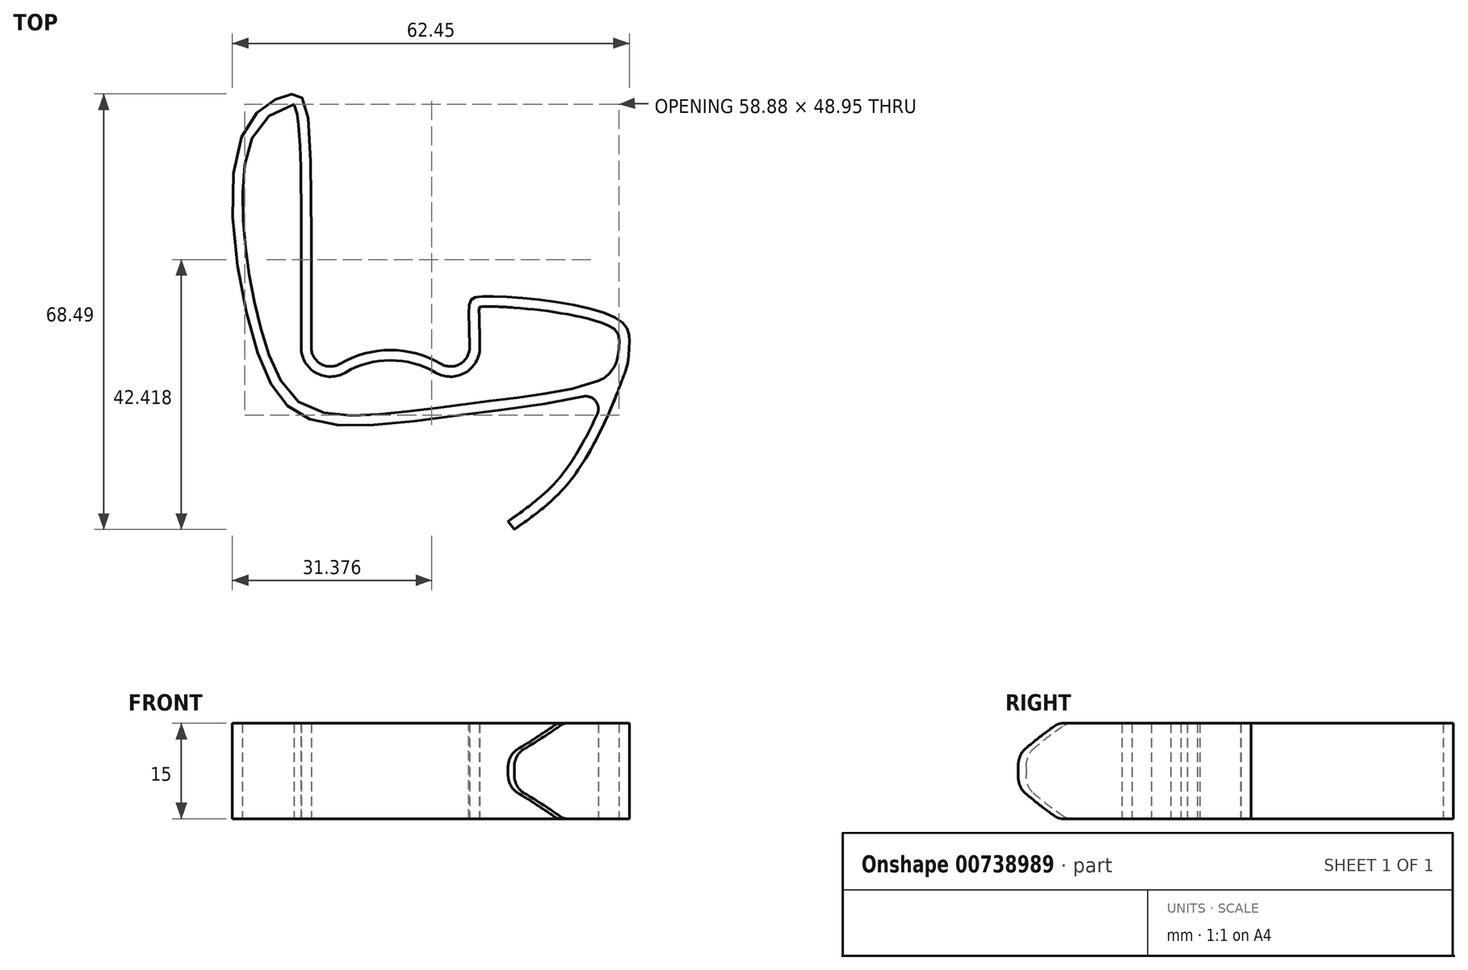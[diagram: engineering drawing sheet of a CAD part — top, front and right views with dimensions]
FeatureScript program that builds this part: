
annotation { "Feature Type Name" : "Feature", "Feature Type Description" : "" }
export const myFeature = defineFeature(function(context is Context, id is Id, definition is map)
    precondition{}
    {
        {
            var Q0;
            Q0=qCreatedBy(makeId("Top.planeOp"),FACE);
            var sketch = newSketch(context, id + "F0", { "sketchPlane" : qUnion([Q0])});
            skLineSegment(sketch, "E0", {"start": v(0, 0) * mm, "end": v(0, 50) * mm});
            skLineSegment(sketch, "E1", {"start": v(0, 50) * mm, "end": v(0, 0) * mm});
            skLineSegment(sketch, "E2", {"start": v(24.9, 0) * mm, "end": v(0, 0) * mm});
            skLineSegment(sketch, "E3", {"start": v(24.9, 0) * mm, "end": v(24.9, 8) * mm});
            skLineSegment(sketch, "E4", {"start": v(24.9, 8) * mm, "end": v(74.9, 8) * mm});
            skSolve(sketch);
        }
        {
            var Q0;
            Q0=qCreatedBy(makeId("Top.planeOp"),FACE);
            var sketch = newSketch(context, id + "F1", { "sketchPlane" : qUnion([Q0])});
            skFitSpline(sketch, "E5", {"points": [v(0, 0) * mm, v(-3.88, 39.66) * mm, v(-10.88, 33.3) * mm, v(-8.75, 0) * mm, v(0, -11.4) * mm, v(24.9, -10.43) * mm, v(48.36, -5.23) * mm, v(50, 0) * mm, v(48.36, 4.37) * mm, v(26.76, 8) * mm, v(24.9, 0) * mm], "startDerivative": vector(0, 727.82) * mm, "endDerivative": vector(0, -307.1) * mm});
            skLineSegment(sketch, "E6", {"start": v(0, 0) * mm, "end": v(0, 0) * mm});
            skLineSegment(sketch, "E7", {"start": v(24.9, 0) * mm, "end": v(24.9, 0) * mm});
            skPoint(sketch, "E8.visualSharp", {"position": v(24.9, -5) * mm});
            skArc(sketch, "E8.filletArc", {"start": v(20.38, -2.58) * mm, "mid": v(23.39, -2.6) * mm, "end": v(24.9, 0) * mm});
            skPoint(sketch, "E9.visualSharp", {"position": v(0, -5) * mm});
            skArc(sketch, "E9.filletArc", {"start": v(0, 0) * mm, "mid": v(1.51, -2.6) * mm, "end": v(4.52, -2.58) * mm});
            skArc(sketch, "E10", {"start": v(20.38, -2.58) * mm, "mid": v(12.45, -0.42) * mm, "end": v(4.52, -2.58) * mm});
            skLineSegment(sketch, "E11", {"start": v(48.36, -5.23) * mm, "end": v(48.36, 4.37) * mm, "construction": true});
            skLineSegment(sketch, "E12", {"start": v(0, 0) * mm, "end": v(24.9, 0) * mm, "construction": true});
            skSolve(sketch);
        }
        {
            var Q0;
            Q0=makeQuery(id+"F1.imprint","IMPRINT",FACE,{"disambiguationData":[TD([[makeQuery(id+"F1.imprint","IMPRINT",EDGE,{"derivedFrom":sQuery(id+"F1.wireOp",EDGE,"E5")}),1.0]])]});
            extrude(context, id + "F2", {"entities" : qUnion([Q0]), "endBound" : BoundingType.SYMMETRIC, "depth" : 15 * mm, "offsetDistance" : 25 * mm});
        }
        {
            var Q0;
            Q0=makeQuery(id+"F2.opExtrude","CAP_FACE",FACE,{"disambiguationData":[OSD([sQuery(id+"F1.wireOp",EDGE,"E5"),sQuery(id+"F1.wireOp",EDGE,"E6"),sQuery(id+"F1.wireOp",EDGE,"E7"),sQuery(id+"F1.wireOp",EDGE,"E8.filletArc"),sQuery(id+"F1.wireOp",EDGE,"E9.filletArc"),sQuery(id+"F1.wireOp",EDGE,"E10")])],"isStart":false});
            var Q1;
            Q1=makeQuery(id+"F2.opExtrude","CAP_FACE",FACE,{"disambiguationData":[OSD([sQuery(id+"F1.wireOp",EDGE,"E5"),sQuery(id+"F1.wireOp",EDGE,"E6"),sQuery(id+"F1.wireOp",EDGE,"E7"),sQuery(id+"F1.wireOp",EDGE,"E8.filletArc"),sQuery(id+"F1.wireOp",EDGE,"E9.filletArc"),sQuery(id+"F1.wireOp",EDGE,"E10")])],"isStart":true});
            shell(context, id + "F3", {"entities" : qUnion([Q0, Q1]), "thickness" : 1.6 * mm});
        }
        {
            var Q0;
            Q0=qCreatedBy(makeId("Front.planeOp"),FACE);
            var sketch = newSketch(context, id + "F4", { "sketchPlane" : qUnion([Q0])});
            skLineSegment(sketch, "E13", {"start": v(51, -8) * mm, "end": v(51, 8) * mm});
            skLineSegment(sketch, "E14", {"start": v(51, 8) * mm, "end": v(28, 0) * mm});
            skLineSegment(sketch, "E15", {"start": v(28, 0) * mm, "end": v(51, -8) * mm});
            skSolve(sketch);
        }
        {
            var Q0;
            Q0=qCreatedBy(makeId("Top.planeOp"),FACE);
            var sketch = newSketch(context, id + "F5", { "sketchPlane" : qUnion([Q0])});
            skFitSpline(sketch, "E16", {"points": [v(50, 0) * mm, v(43.14, -17.48) * mm, v(31.93, -28.63) * mm], "startDerivative": vector(-0.86, -22.29) * mm, "endDerivative": vector(-34.8, -24.25) * mm});
            skSolve(sketch);
        }
        {
            var Q0;
            Q0=qCreatedBy(makeId("Front.planeOp"),FACE);
            var sketch = newSketch(context, id + "F6", { "sketchPlane" : qUnion([Q0])});
            skLineSegment(sketch, "E17", {"start": v(50, -7.5) * mm, "end": v(50, 7.5) * mm});
            skLineSegment(sketch, "E18", {"start": v(50, 7.5) * mm, "end": v(48.4, 7.5) * mm});
            skLineSegment(sketch, "E19", {"start": v(48.4, 7.5) * mm, "end": v(48.4, -7.5) * mm});
            skLineSegment(sketch, "E20", {"start": v(48.4, -7.5) * mm, "end": v(50, -7.5) * mm});
            skSolve(sketch);
        }
        {
            var Q0;
            Q0=makeQuery(id+"F6.imprint","IMPRINT",FACE,{"disambiguationData":[TD([[makeQuery(id+"F6.imprint","IMPRINT",EDGE,{"derivedFrom":sQuery(id+"F6.wireOp",EDGE,"E17")}),1.0]])]});
            var Q1;
            Q1=sQuery(id+"F5.wireOp",EDGE,"E16");
            sweep(context, id + "F7", {"operationType" : NewBodyOperationType.ADD, "profiles" : qUnion([Q0]), "path" : qUnion([Q1])});
        }
        {
            var Q0;
            Q0=makeQuery(id+"F7.opSweep","CAP_EDGE",EDGE,{"disambiguationData":[OSD([sQuery(id+"F5.wireOp",VERTEX,"E16.end"),sQuery(id+"F6.wireOp",EDGE,"E20")])],"isStart":false});
            var Q1;
            Q1=makeQuery(id+"F7.opSweep","CAP_EDGE",EDGE,{"disambiguationData":[OSD([sQuery(id+"F5.wireOp",VERTEX,"E16.end"),sQuery(id+"F6.wireOp",EDGE,"E18")])],"isStart":false});
            chamfer(context, id + "F8", {"entities" : qUnion([Q0, Q1]), "chamferType" : ChamferType.TWO_OFFSETS, "width1" : 5 * mm, "oppositeDirection" : false, "width2" : 10 * mm, "tangentPropagation" : true});
        }
        {
            var Q0;
            {var subQ0=sQuery(id+"F6.wireOp",EDGE,"E20");Q0=makeQuery(id+"F8.opChamfer","BLEND_EDGE",EDGE,{"blendedFrom":[makeQuery(id+"F7.opSweep","CAP_EDGE",EDGE,{"disambiguationData":[OSD([sQuery(id+"F5.wireOp",VERTEX,"E16.end"),subQ0])],"isStart":false}),makeQuery(id+"F7.boolean.opBoolean","MERGE",FACE,{"derivedFrom":[makeQuery(id+"F2.opExtrude","CAP_FACE",FACE,{"disambiguationData":[OSD([sQuery(id+"F1.wireOp",EDGE,"E5"),sQuery(id+"F1.wireOp",EDGE,"E6"),sQuery(id+"F1.wireOp",EDGE,"E7"),sQuery(id+"F1.wireOp",EDGE,"E8.filletArc"),sQuery(id+"F1.wireOp",EDGE,"E9.filletArc"),sQuery(id+"F1.wireOp",EDGE,"E10")])],"isStart":true}),makeQuery(id+"F7.opSweep","SWEPT_FACE",FACE,{"disambiguationData":[OSD([sQuery(id+"F5.wireOp",EDGE,"E16"),subQ0])]})]})],"blendedInto":[makeQuery(id+"F7.boolean.opBoolean","MERGE",FACE,{"derivedFrom":[makeQuery(id+"F2.opExtrude","CAP_FACE",FACE,{"disambiguationData":[OSD([sQuery(id+"F1.wireOp",EDGE,"E5"),sQuery(id+"F1.wireOp",EDGE,"E6"),sQuery(id+"F1.wireOp",EDGE,"E7"),sQuery(id+"F1.wireOp",EDGE,"E8.filletArc"),sQuery(id+"F1.wireOp",EDGE,"E9.filletArc"),sQuery(id+"F1.wireOp",EDGE,"E10")])],"isStart":true}),makeQuery(id+"F7.opSweep","SWEPT_FACE",FACE,{"disambiguationData":[OSD([sQuery(id+"F5.wireOp",EDGE,"E16"),subQ0])]})]})]});}
            var Q1;
            {var subQ0=sQuery(id+"F6.wireOp",EDGE,"E20");var subQ1=sQuery(id+"F5.wireOp",VERTEX,"E16.end");Q1=makeQuery(id+"F8.opChamfer","BLEND_EDGE",EDGE,{"blendedFrom":[makeQuery(id+"F7.opSweep","CAP_EDGE",EDGE,{"disambiguationData":[OSD([subQ1,subQ0])],"isStart":false}),makeQuery(id+"F7.opSweep","CAP_FACE",FACE,{"disambiguationData":[OSD([subQ1,sQuery(id+"F6.wireOp",EDGE,"E17"),sQuery(id+"F6.wireOp",EDGE,"E18"),sQuery(id+"F6.wireOp",EDGE,"E19"),subQ0])],"isStart":false})],"blendedInto":[makeQuery(id+"F7.opSweep","CAP_FACE",FACE,{"disambiguationData":[OSD([subQ1,sQuery(id+"F6.wireOp",EDGE,"E17"),sQuery(id+"F6.wireOp",EDGE,"E18"),sQuery(id+"F6.wireOp",EDGE,"E19"),subQ0])],"isStart":false})]});}
            var Q2;
            {var subQ0=sQuery(id+"F6.wireOp",EDGE,"E18");var subQ1=sQuery(id+"F5.wireOp",VERTEX,"E16.end");Q2=makeQuery(id+"F8.opChamfer","BLEND_EDGE",EDGE,{"blendedFrom":[makeQuery(id+"F7.opSweep","CAP_EDGE",EDGE,{"disambiguationData":[OSD([subQ1,subQ0])],"isStart":false}),makeQuery(id+"F7.opSweep","CAP_FACE",FACE,{"disambiguationData":[OSD([subQ1,sQuery(id+"F6.wireOp",EDGE,"E17"),subQ0,sQuery(id+"F6.wireOp",EDGE,"E19"),sQuery(id+"F6.wireOp",EDGE,"E20")])],"isStart":false})],"blendedInto":[makeQuery(id+"F7.opSweep","CAP_FACE",FACE,{"disambiguationData":[OSD([subQ1,sQuery(id+"F6.wireOp",EDGE,"E17"),subQ0,sQuery(id+"F6.wireOp",EDGE,"E19"),sQuery(id+"F6.wireOp",EDGE,"E20")])],"isStart":false})]});}
            var Q3;
            {var subQ0=sQuery(id+"F6.wireOp",EDGE,"E18");Q3=makeQuery(id+"F8.opChamfer","BLEND_EDGE",EDGE,{"blendedFrom":[makeQuery(id+"F7.opSweep","CAP_EDGE",EDGE,{"disambiguationData":[OSD([sQuery(id+"F5.wireOp",VERTEX,"E16.end"),subQ0])],"isStart":false}),makeQuery(id+"F7.boolean.opBoolean","MERGE",FACE,{"derivedFrom":[makeQuery(id+"F2.opExtrude","CAP_FACE",FACE,{"disambiguationData":[OSD([sQuery(id+"F1.wireOp",EDGE,"E5"),sQuery(id+"F1.wireOp",EDGE,"E6"),sQuery(id+"F1.wireOp",EDGE,"E7"),sQuery(id+"F1.wireOp",EDGE,"E8.filletArc"),sQuery(id+"F1.wireOp",EDGE,"E9.filletArc"),sQuery(id+"F1.wireOp",EDGE,"E10")])],"isStart":false}),makeQuery(id+"F7.opSweep","SWEPT_FACE",FACE,{"disambiguationData":[OSD([sQuery(id+"F5.wireOp",EDGE,"E16"),subQ0])]})]})],"blendedInto":[makeQuery(id+"F7.boolean.opBoolean","MERGE",FACE,{"derivedFrom":[makeQuery(id+"F2.opExtrude","CAP_FACE",FACE,{"disambiguationData":[OSD([sQuery(id+"F1.wireOp",EDGE,"E5"),sQuery(id+"F1.wireOp",EDGE,"E6"),sQuery(id+"F1.wireOp",EDGE,"E7"),sQuery(id+"F1.wireOp",EDGE,"E8.filletArc"),sQuery(id+"F1.wireOp",EDGE,"E9.filletArc"),sQuery(id+"F1.wireOp",EDGE,"E10")])],"isStart":false}),makeQuery(id+"F7.opSweep","SWEPT_FACE",FACE,{"disambiguationData":[OSD([sQuery(id+"F5.wireOp",EDGE,"E16"),subQ0])]})]})]});}
            fillet(context, id + "F9", {"entities" : qUnion([Q0, Q1, Q2, Q3]), "radius" : 3 * mm, "tangentPropagation" : true, "allowEdgeOverflow" : false});
        }
        {
            var Q0;
            Q0=makeQuery(id+"F7.boolean.opBoolean","INTERSECT",EDGE,{"derivedFrom":[makeQuery(id+"F2.opExtrude","SWEPT_FACE",FACE,{"disambiguationData":[OSD([sQuery(id+"F1.wireOp",EDGE,"E5")])]}),makeQuery(id+"F7.opSweep","SWEPT_FACE",FACE,{"disambiguationData":[OSD([sQuery(id+"F5.wireOp",EDGE,"E16"),sQuery(id+"F6.wireOp",EDGE,"E19")])]})]});
            fillet(context, id + "F10", {"entities" : qUnion([Q0]), "radius" : 2 * mm, "tangentPropagation" : true, "allowEdgeOverflow" : false});
        }
        {
            var Q0;
            Q0=makeQuery(id+"F7.boolean.opBoolean","INTERSECT",EDGE,{"derivedFrom":[makeQuery(id+"F2.opExtrude","SWEPT_FACE",FACE,{"disambiguationData":[OSD([sQuery(id+"F1.wireOp",EDGE,"E5")])]}),makeQuery(id+"F7.opSweep","SWEPT_FACE",FACE,{"disambiguationData":[OSD([sQuery(id+"F5.wireOp",EDGE,"E16"),sQuery(id+"F6.wireOp",EDGE,"E17")])]})]});
            fillet(context, id + "F11", {"entities" : qUnion([Q0]), "radius" : 200 * mm, "tangentPropagation" : true, "allowEdgeOverflow" : false});
        }
        {
            var Q0;
            Q0=makeQuery(id+"F7.boolean.opBoolean","INTERSECT",EDGE,{"disambiguationData":[OD(0.0)],"derivedFrom":[makeQuery(id+"F3.opShell","OFFSET_FACE",FACE,{"disambiguationData":[OSD([sQuery(id+"F1.wireOp",EDGE,"E5")]),OD(2.0)]}),makeQuery(id+"F7.opSweep","SWEPT_FACE",FACE,{"disambiguationData":[OSD([sQuery(id+"F5.wireOp",EDGE,"E16"),sQuery(id+"F6.wireOp",EDGE,"E19")])]})]});
            fillet(context, id + "F12", {"entities" : qUnion([Q0]), "radius" : 5 * mm, "tangentPropagation" : true, "allowEdgeOverflow" : false});
        }
    });
